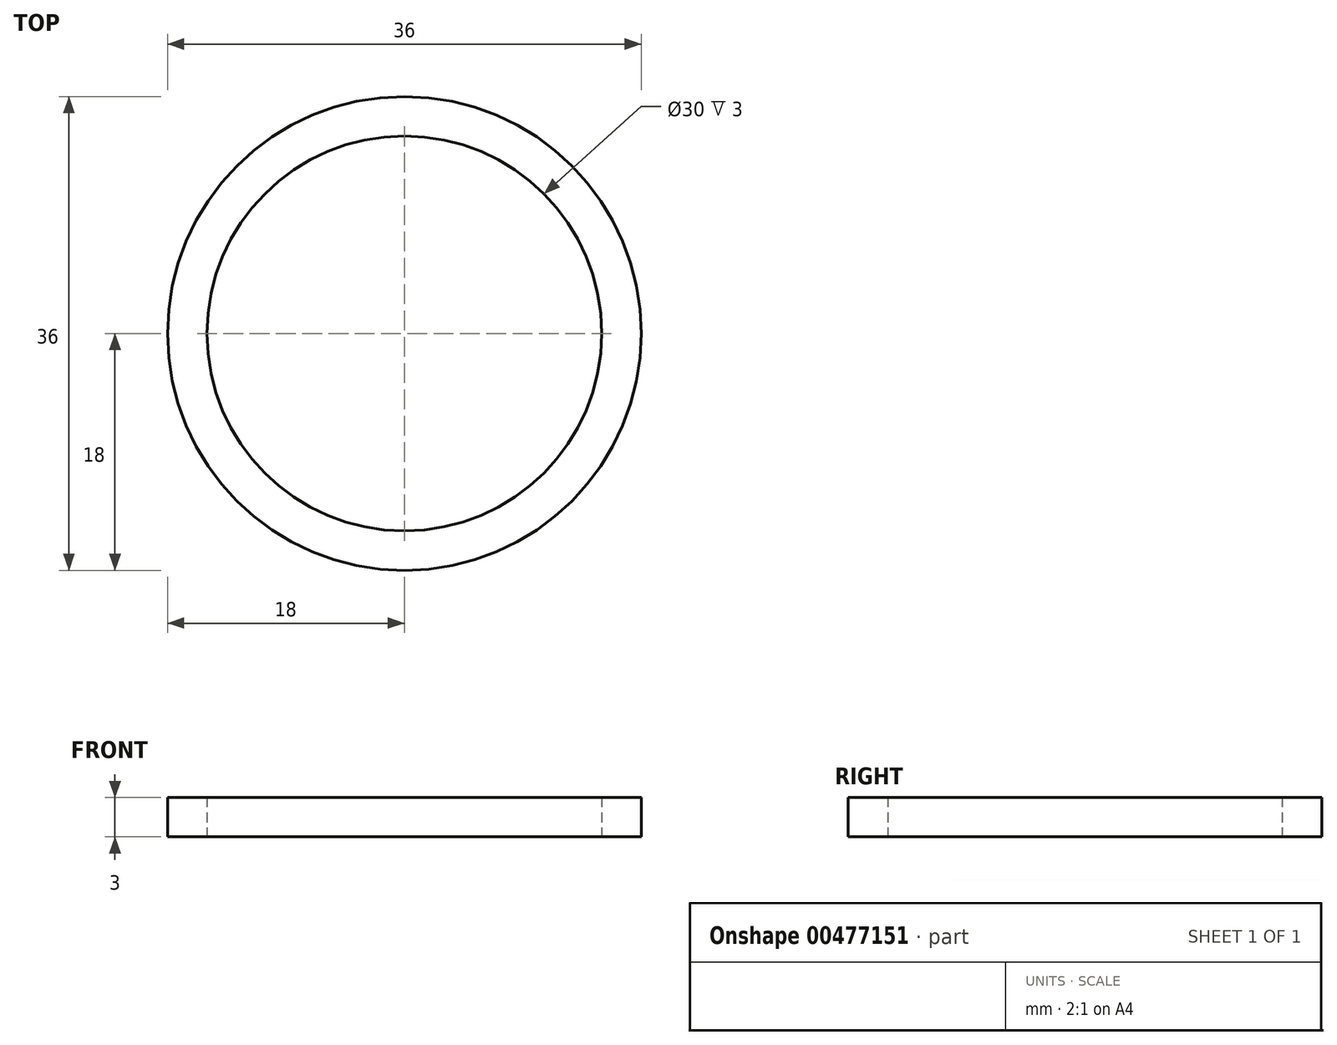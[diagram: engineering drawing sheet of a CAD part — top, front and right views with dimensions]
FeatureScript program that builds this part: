
annotation { "Feature Type Name" : "Feature", "Feature Type Description" : "" }
export const myFeature = defineFeature(function(context is Context, id is Id, definition is map)
    precondition{}
    {
        {
            var Q0;
            Q0=qCreatedBy(makeId("Top.planeOp"),FACE);
            var sketch = newSketch(context, id + "F0", { "sketchPlane" : qUnion([Q0])});
            skCircle(sketch, "E0", {"center": v(0, 0) * mm, "radius": 18 * mm});
            skCircle(sketch, "E1", {"center": v(0, 0) * mm, "radius": 15 * mm});
            skCircle(sketch, "E2", {"center": v(0, 0) * mm, "radius": 11 * mm});
            skSolve(sketch);
        }
        {
            var Q0;
            Q0 = qSketchRegion(id + "F0", true);
            extrude(context, id + "F1", {"entities" : qUnion([Q0]), "depth" : 3 * mm});
        }
        {
            var Q0;
            Q0=sQuery(id+"F0.wireOp",EDGE,"E2");
            extrude(context, id + "F2", {"bodyType" : ToolBodyType.SURFACE, "surfaceEntities" : qUnion([Q0]), "depth" : 5 * mm});
        }
        {
            var Q0;
            Q0=sQuery(id+"F0.wireOp",EDGE,"E1");
            extrude(context, id + "F3", {"bodyType" : ToolBodyType.SURFACE, "surfaceEntities" : qUnion([Q0]), "depth" : 7.5 * mm});
        }
    });
